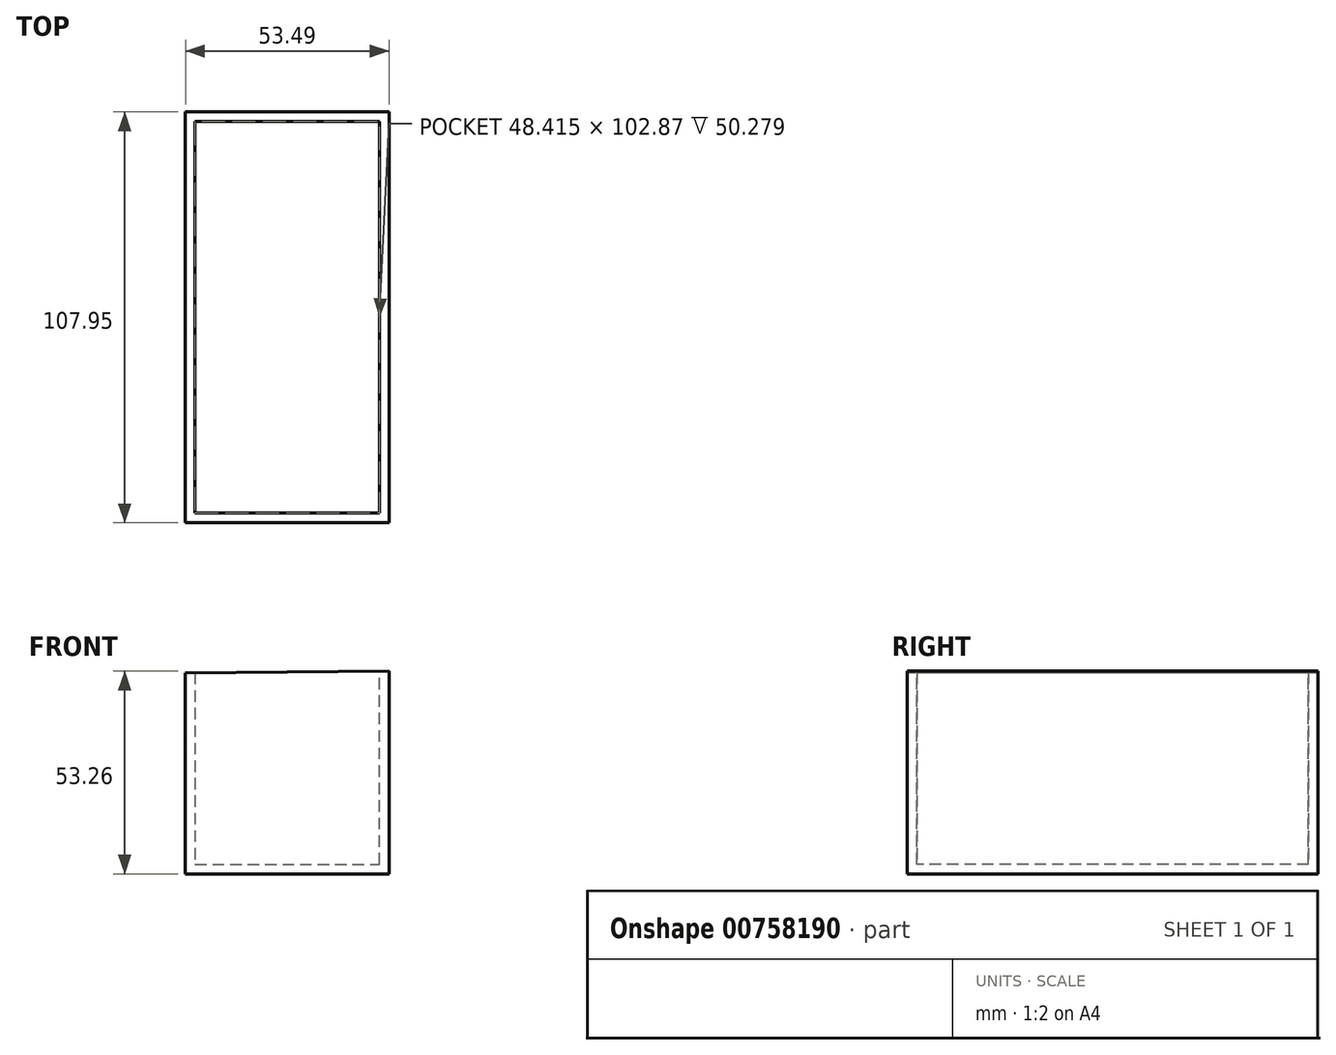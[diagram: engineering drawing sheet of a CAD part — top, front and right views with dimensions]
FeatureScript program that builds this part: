
annotation { "Feature Type Name" : "Feature", "Feature Type Description" : "" }
export const myFeature = defineFeature(function(context is Context, id is Id, definition is map)
    precondition{}
    {
        {
            var Q0;
            Q0=qCreatedBy(makeId("Front.planeOp"),FACE);
            var sketch = newSketch(context, id + "F0", { "sketchPlane" : qUnion([Q0])});
            skLineSegment(sketch, "E0", {"start": v(-42.91, 25.24) * mm, "end": v(-42.91, -27.56) * mm});
            skLineSegment(sketch, "E1", {"start": v(-42.91, -27.56) * mm, "end": v(10.58, -27.56) * mm});
            skLineSegment(sketch, "E2", {"start": v(10.58, -27.56) * mm, "end": v(10.58, 25.7) * mm});
            skLineSegment(sketch, "E3", {"start": v(10.58, 25.7) * mm, "end": v(-42.91, 25.24) * mm});
            skSolve(sketch);
        }
        {
            var Q0;
            Q0 = qSketchRegion(id + "F0", true);
            extrude(context, id + "F1", {"entities" : qUnion([Q0]), "oppositeDirection" : true, "depth" : 107.95 * mm, "offsetDistance" : 25.4 * mm});
        }
        {
            var Q0;
            Q0=makeQuery(id+"F1.opExtrude","SWEPT_FACE",FACE,{"disambiguationData":[OSD([sQuery(id+"F0.wireOp",EDGE,"E3")])]});
            shell(context, id + "F2", {"entities" : qUnion([Q0]), "thickness" : 2.54 * mm});
        }
    });
